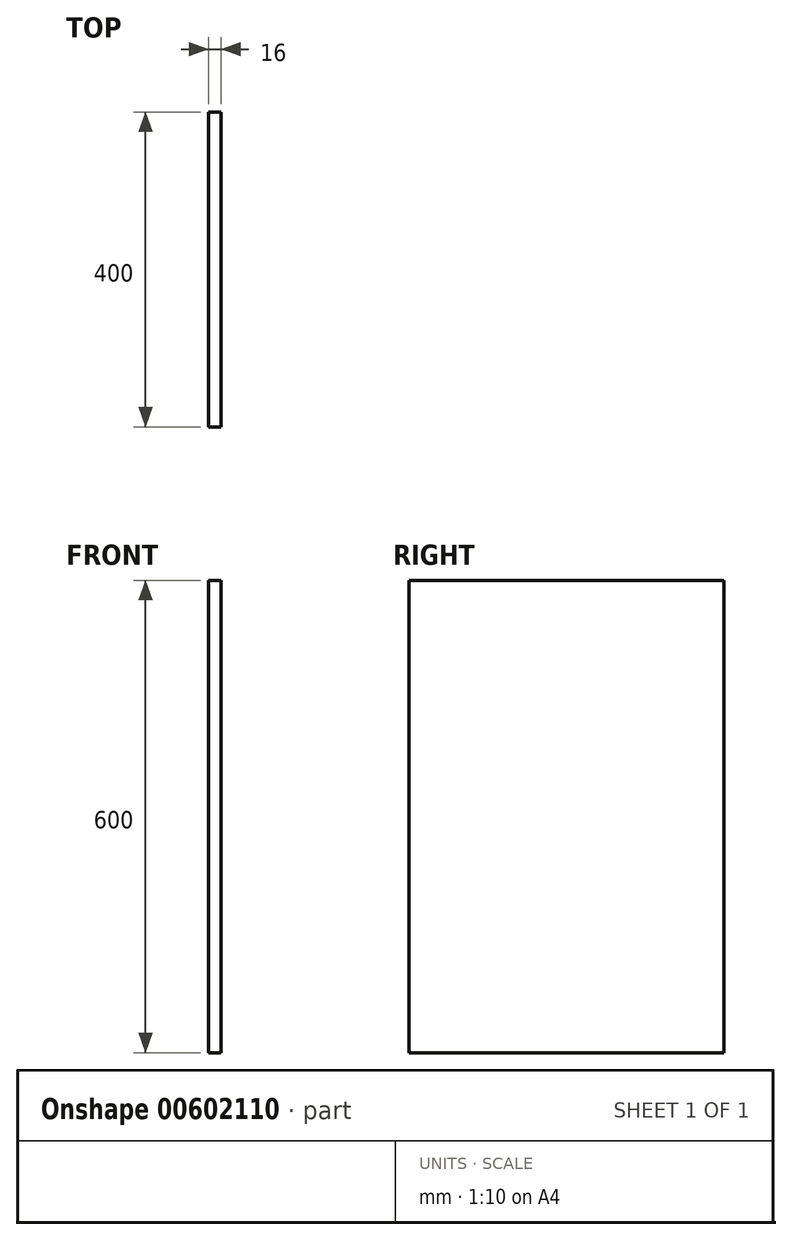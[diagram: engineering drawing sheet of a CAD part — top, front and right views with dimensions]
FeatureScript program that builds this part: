
annotation { "Feature Type Name" : "Feature", "Feature Type Description" : "" }
export const myFeature = defineFeature(function(context is Context, id is Id, definition is map)
    precondition{}
    {
        {
            var Q0;
            Q0=qCreatedBy(makeId("Right.planeOp"),FACE);
            var sketch = newSketch(context, id + "F0", { "sketchPlane" : qUnion([Q0])});
            skLineSegment(sketch, "E0.bottom", {"start": v(0, 0) * mm, "end": v(-400, 0) * mm});
            skLineSegment(sketch, "E0.top", {"start": v(0, 600) * mm, "end": v(-400, 600) * mm});
            skLineSegment(sketch, "E0.left", {"start": v(0, 0) * mm, "end": v(0, 600) * mm});
            skLineSegment(sketch, "E0.right", {"start": v(-400, 0) * mm, "end": v(-400, 600) * mm});
            skSolve(sketch);
        }
        {
            var Q0;
            Q0 = qSketchRegion(id + "F0", true);
            extrude(context, id + "F1", {"entities" : qUnion([Q0]), "depth" : 16 * mm, "offsetDistance" : 25 * mm});
        }
    });
